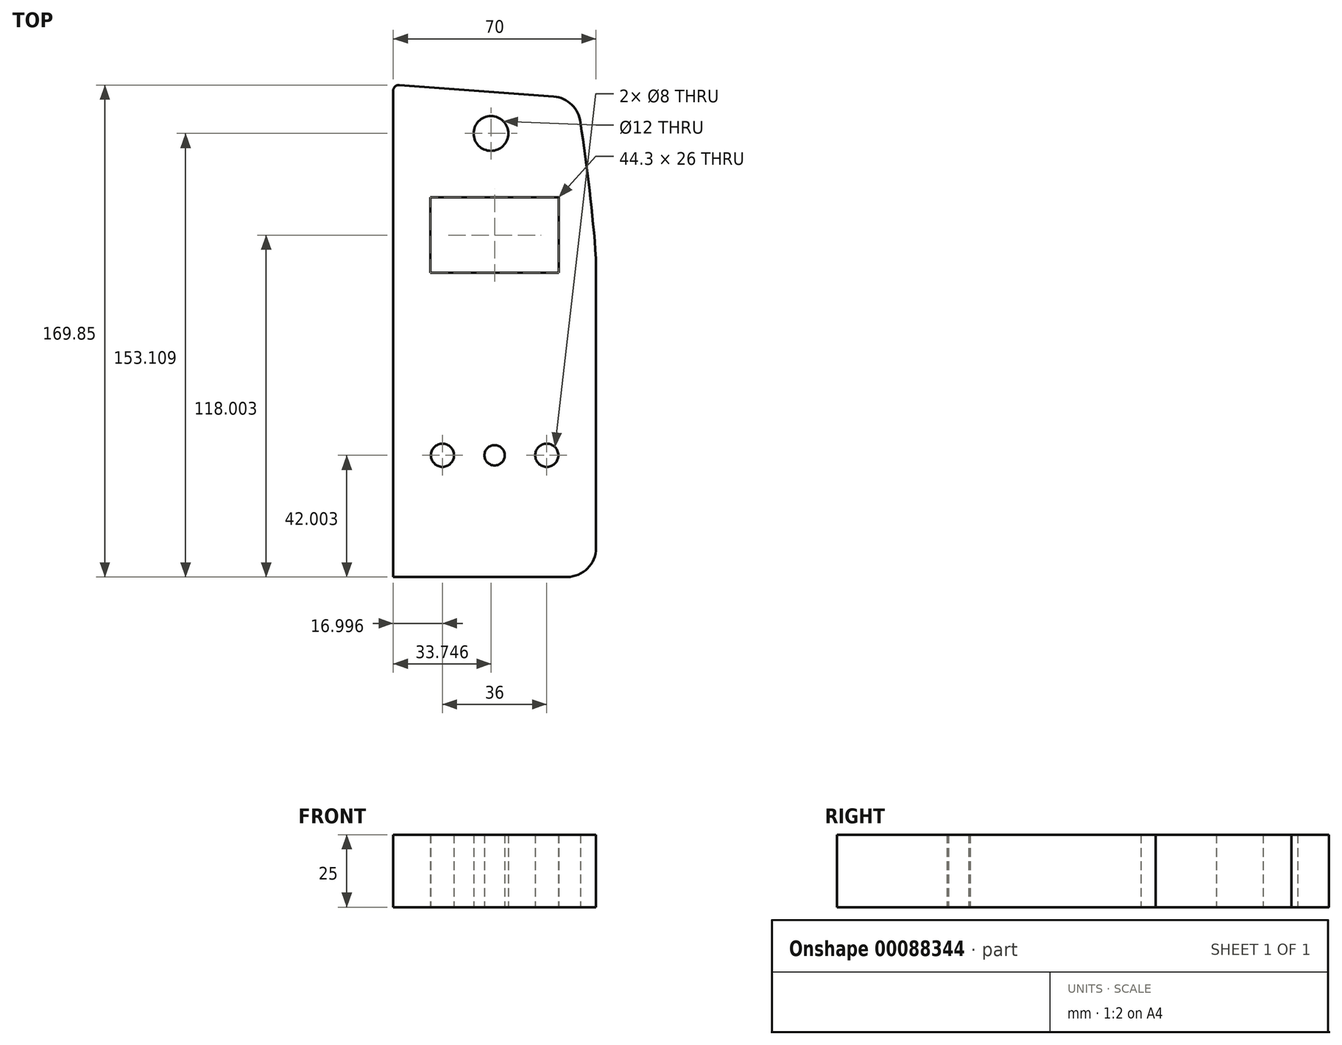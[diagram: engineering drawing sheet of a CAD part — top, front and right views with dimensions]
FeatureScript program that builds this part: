
annotation { "Feature Type Name" : "Feature", "Feature Type Description" : "" }
export const myFeature = defineFeature(function(context is Context, id is Id, definition is map)
    precondition{}
    {
        {
            var Q0;
            Q0=qCreatedBy(makeId("Top.planeOp"),FACE);
            var sketch = newSketch(context, id + "F0", { "sketchPlane" : qUnion([Q0])});
            skLineSegment(sketch, "E0", {"start": v(-42.1, -71.43) * mm, "end": v(17.9, -71.43) * mm});
            skLineSegment(sketch, "E1", {"start": v(-42.1, -71.43) * mm, "end": v(-42.1, 96.42) * mm});
            skLineSegment(sketch, "E2", {"start": v(27.9, -61.43) * mm, "end": v(27.9, 38.57) * mm});
            skLineSegment(sketch, "E3", {"start": v(13.3, 94.41) * mm, "end": v(-39.94, 98.41) * mm});
            skPoint(sketch, "E4.visualSharp", {"position": v(-42.1, 98.57) * mm});
            skArc(sketch, "E4.filletArc", {"start": v(-39.94, 98.41) * mm, "mid": v(-41.45, 97.88) * mm, "end": v(-42.1, 96.42) * mm});
            skPoint(sketch, "E5.visualSharp", {"position": v(21.67, 93.78) * mm});
            skArc(sketch, "E5.filletArc", {"start": v(22.5, 85.45) * mm, "mid": v(19.53, 91.6) * mm, "end": v(13.3, 94.41) * mm});
            skPoint(sketch, "E6.visualSharp", {"position": v(27.9, -71.43) * mm});
            skArc(sketch, "E6.filletArc", {"start": v(17.9, -71.43) * mm, "mid": v(24.98, -68.5) * mm, "end": v(27.9, -61.43) * mm});
            skArc(sketch, "E7", {"start": v(27.9, 38.57) * mm, "mid": v(25.67, 62.06) * mm, "end": v(22.5, 85.45) * mm});
            skLineSegment(sketch, "E8.bottom", {"start": v(-29.24, 59.57) * mm, "end": v(15.06, 59.57) * mm});
            skLineSegment(sketch, "E8.top", {"start": v(-29.24, 33.57) * mm, "end": v(15.06, 33.57) * mm});
            skLineSegment(sketch, "E8.left", {"start": v(-29.24, 59.57) * mm, "end": v(-29.24, 33.57) * mm});
            skLineSegment(sketch, "E8.right", {"start": v(15.06, 59.57) * mm, "end": v(15.06, 33.57) * mm});
            skPoint(sketch, "E8.middle", {"position": v(-7.1, 46.57) * mm});
            skLineSegment(sketch, "E9", {"start": v(27.9, -71.43) * mm, "end": v(-42.1, -71.43) * mm, "construction": true});
            skLineSegment(sketch, "E10", {"start": v(-7.1, 33.57) * mm, "end": v(-7.1, -71.43) * mm, "construction": true});
            skLineSegment(sketch, "E11", {"start": v(-7.1, 59.57) * mm, "end": v(-7.1, 90.36) * mm, "construction": true});
            skCircle(sketch, "E12", {"center": v(-8.34, 81.68) * mm, "radius": 6 * mm});
            skCircle(sketch, "E13", {"center": v(-7.1, -29.43) * mm, "radius": 3.5 * mm});
            skCircle(sketch, "E14", {"center": v(-25.1, -29.43) * mm, "radius": 4 * mm});
            skCircle(sketch, "E15.MirrorC", {"center": v(10.9, -29.43) * mm, "radius": 4 * mm});
            skSolve(sketch);
        }
        {
            var Q0;
            Q0=makeQuery(id+"F0.imprint","IMPRINT",FACE,{"disambiguationData":[TD([[makeQuery(id+"F0.imprint","IMPRINT",EDGE,{"derivedFrom":sQuery(id+"F0.wireOp",EDGE,"E0")}),1.0]])]});
            extrude(context, id + "F1", {"entities" : qUnion([Q0]), "depth" : 25 * mm});
        }
    });
